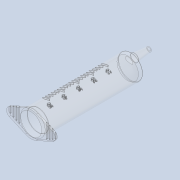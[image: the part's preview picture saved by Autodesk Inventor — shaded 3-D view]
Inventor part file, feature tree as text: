
AUTODESK INVENTOR PART (.ipt)
format: ipt  version: 2020 (Build 240168000, 168)  size: 843,264 bytes
history: native  units: mm
features: sketch x9, extrude x6, plane x4, revolve x3, fillet x2, loft x1, mirror x1, other x1
ambient origin geometry x8: Origin, YZ Plane, XZ Plane, XY Plane, X Axis, Y Axis, Z Axis, Center Point
bodies: Solid1 (feature_tree)
feature tree (27):
  revolve  "Revolution1"  [1 undecoded]
  plane  "Work Plane1"
  loft  "Loft1"
  extrude  "Extrusion1"  Depth=4.0mm
  plane  "Work Plane2"
  revolve  "Revolution2"  Angle=90.0deg
  revolve  "Revolution3"  [1 undecoded]
  fillet  "Fillet1"  Radius=13.0mm
  extrude  "Extrusion2"  Depth=7.0mm
  extrude  "Extrusion3"  Depth=11.0mm
  plane  "Work Plane3"
  extrude  "Extrusion4"  TaperAngle=360.0deg  [1 undecoded]
  extrude  "Extrusion5"  Depth=1.047198mm
  extrude  "Extrusion7"  Depth=0.5mm
  fillet  "Fillet2"  Radius=2.0mm
  mirror  "Mirror1"
  sketch  "Sketch1"  dims[d0=100.0mm d1=2.0mm]
  sketch  "Sketch2"  dims[d2=13.0mm d3=12.5mm]
  other  "Edges1"
  sketch  "Sketch3"  dims[d4=90.0deg d5=4.0mm]
  sketch  "Sketch4"  dims[d7=8.0mm d8=0.0mm d9=90.0deg]
  sketch  "Sketch5"  dims[d10=0.0mm d11=90.0deg d12=15.0mm d13=-1.047198mm d14=13.0mm]
  sketch  "Sketch7"  dims[d15=11.0mm d16=7.0mm]
  sketch  "Sketch8"  dims[d17=0.5mm d18=11.0mm]
  sketch  "Sketch9"  dims[d19=12.217305mm d20=360.0deg]
  sketch  "Sketch11"  dims[d22=90.0deg d24=1.047198mm d25=0.5mm d28=2.0mm d29=0.0mm d30=22.0mm d31=2.0mm d32=0.0mm d33=15.0mm d35=7.5mm d36=0.5mm d38=2.5mm d39=7.5mm d40=2.5mm d41=0.5mm d42=200.0mm d44=3.0mm d45=10.0mm d47=10.0mm d49=50.0mm d51=15.0mm d52=10.0mm d54=10.0mm d56=5.0mm d57=0.0mm d60=5.0mm d61=2.25mm d62=50.0mm d64=15.0mm d65=10.0mm d67=10.0mm d69=5.0mm d70=0.0mm d104=7.0mm d105=7.0mm d106=0.5mm d107=3.0mm d108=6.0mm d109=6.0mm d110=0.5mm d111=3.0mm d112=4.5mm d113=4.5mm d114=0.5mm d115=3.0mm d116=2.5mm d117=2.5mm d118=0.5mm d119=0.75mm d120=0.0mm d121=0.5mm]
  plane  "Work Plane4"
note: 3 required parameter values undecoded (feature->parameter linkage not recoverable at this tier; creation-order binding heuristic only, values carry confidence <= 0.55)